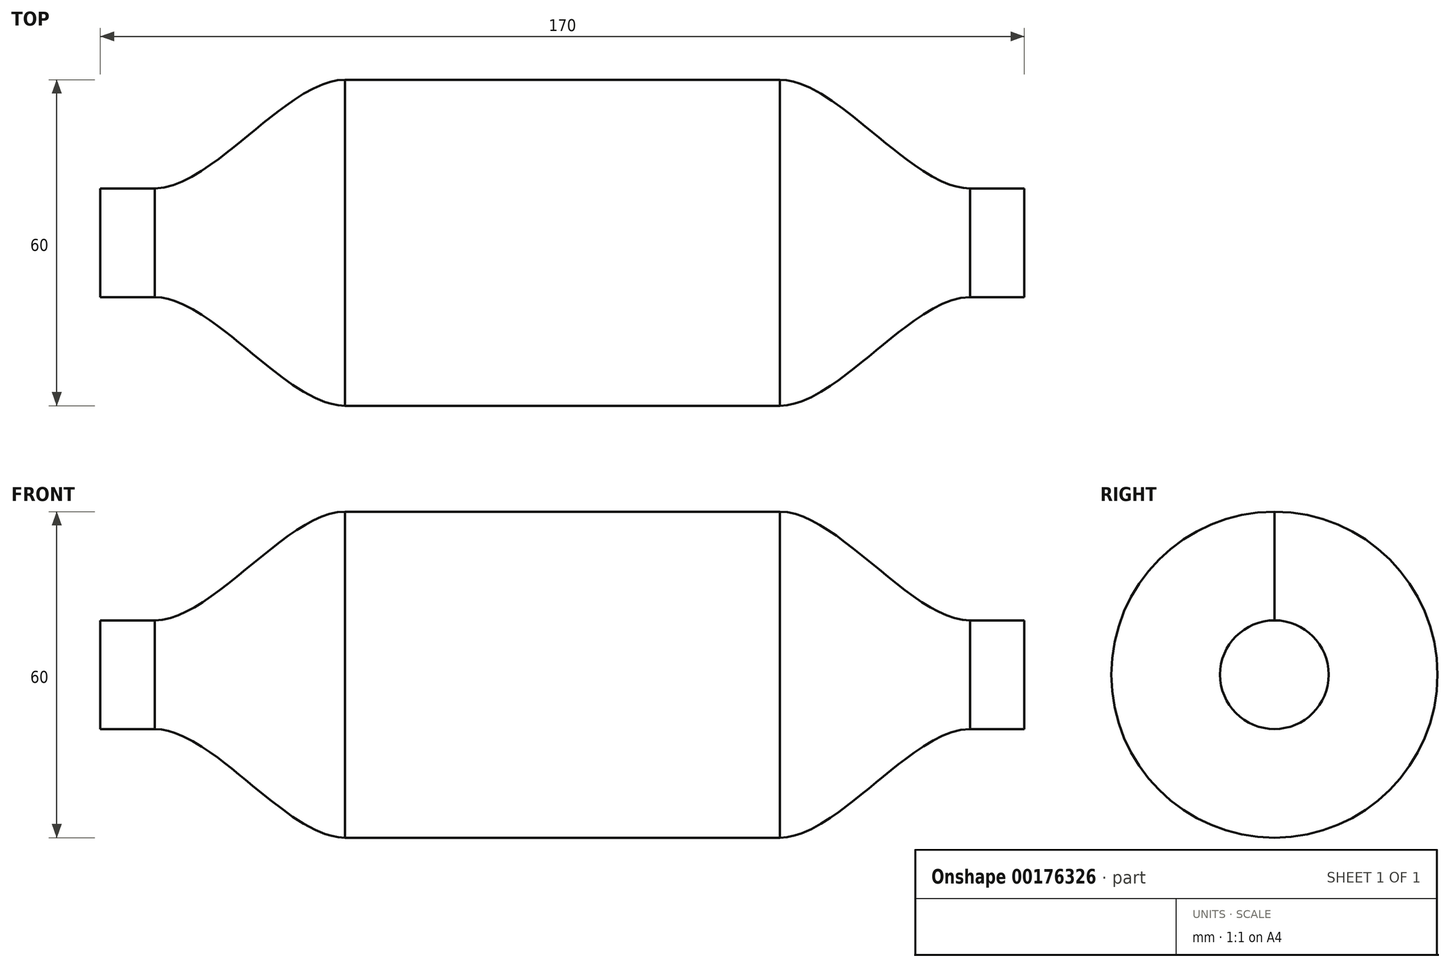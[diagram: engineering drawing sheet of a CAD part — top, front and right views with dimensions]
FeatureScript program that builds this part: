
annotation { "Feature Type Name" : "Feature", "Feature Type Description" : "" }
export const myFeature = defineFeature(function(context is Context, id is Id, definition is map)
    precondition{}
    {
        {
            var Q0;
            Q0=qCreatedBy(makeId("Top.planeOp"),FACE);
            var sketch = newSketch(context, id + "F0", { "sketchPlane" : qUnion([Q0])});
            skLineSegment(sketch, "E0", {"start": v(-46.54, 10) * mm, "end": v(-36.54, 10) * mm});
            skLineSegment(sketch, "E1", {"start": v(123.46, 10) * mm, "end": v(113.46, 10) * mm});
            skLineSegment(sketch, "E2", {"start": v(-113.84, 0) * mm, "end": v(145.76, 0) * mm});
            skLineSegment(sketch, "E3", {"start": v(-1.54, 30) * mm, "end": v(78.46, 30) * mm});
            skFitSpline(sketch, "E4", {"points": [v(78.46, 30) * mm, v(113.46, 10) * mm], "startDerivative": vector(32.02, 0) * mm, "endDerivative": vector(32.02, 0) * mm});
            skFitSpline(sketch, "E5", {"points": [v(-1.54, 30) * mm, v(-36.54, 10) * mm], "startDerivative": vector(-32.02, 0) * mm, "endDerivative": vector(-32.02, 0) * mm});
            skLineSegment(sketch, "E6", {"start": v(123.46, 10) * mm, "end": v(123.46, 0) * mm});
            skLineSegment(sketch, "E7", {"start": v(-46.54, 10) * mm, "end": v(-46.54, 0) * mm});
            skSolve(sketch);
        }
        {
            var Q0;
            Q0=makeQuery(id+"F0.imprint","IMPRINT",FACE,{"disambiguationData":[TD([[makeQuery(id+"F0.imprint","IMPRINT",EDGE,{"derivedFrom":sQuery(id+"F0.wireOp",EDGE,"E0")}),-1.0]])]});
            var Q1;
            Q1=sQuery(id+"F0.wireOp",EDGE,"E2");
            revolve(context, id + "F1", {"entities" : qUnion([Q0]), "axis" : qUnion([Q1]), "revolveType" : RevolveType.FULL});
        }
    });
